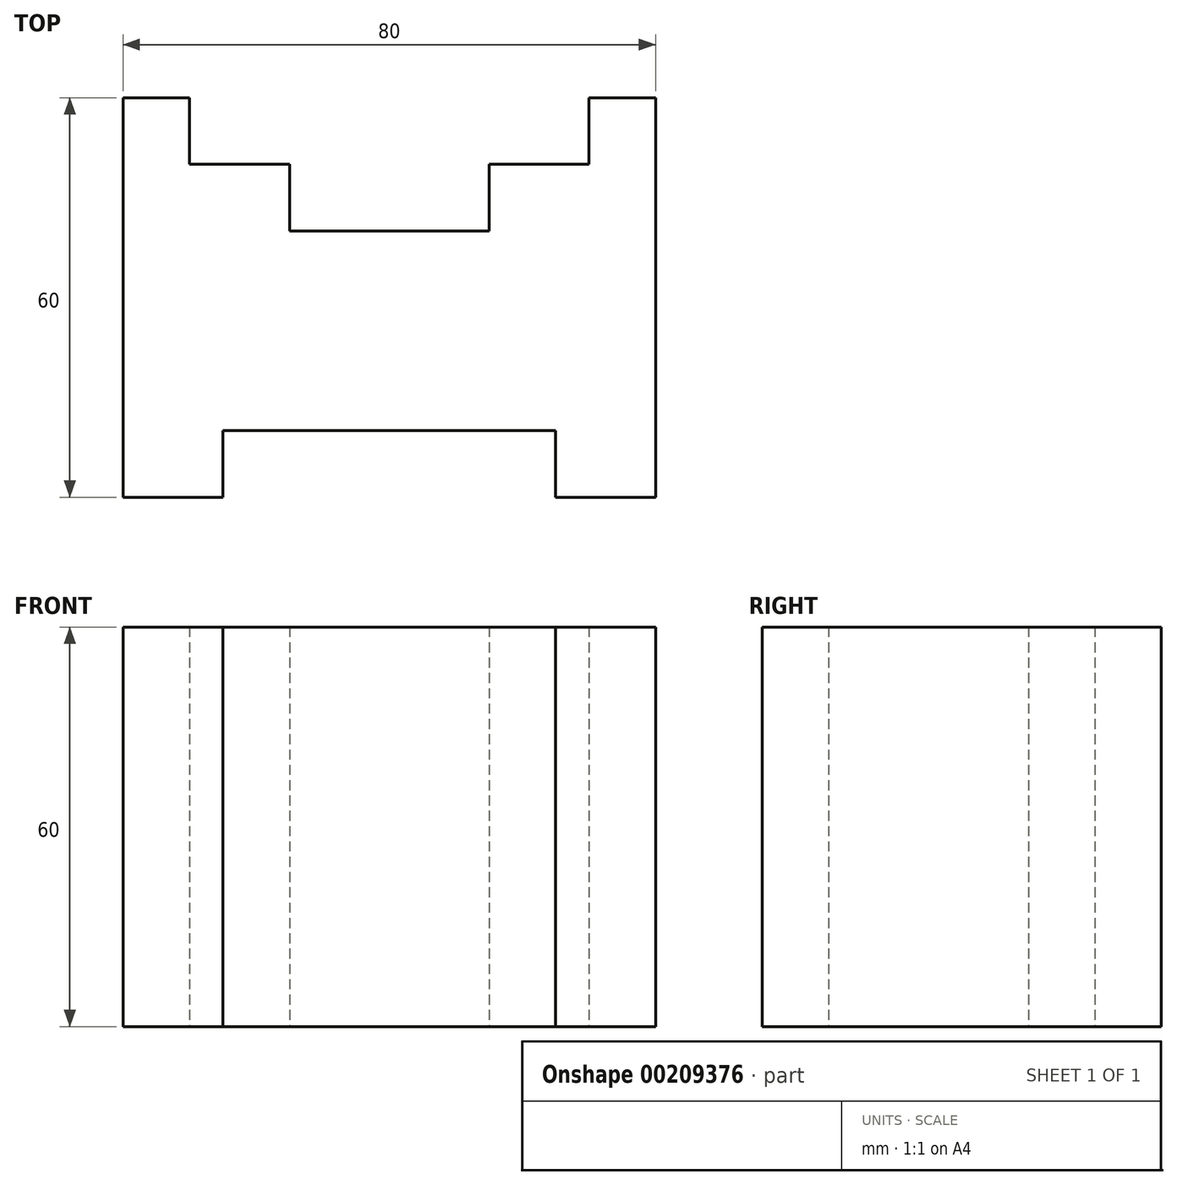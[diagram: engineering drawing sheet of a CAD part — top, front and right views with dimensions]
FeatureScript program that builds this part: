
annotation { "Feature Type Name" : "Feature", "Feature Type Description" : "" }
export const myFeature = defineFeature(function(context is Context, id is Id, definition is map)
    precondition{}
    {
        {
            var Q0;
            Q0=qCreatedBy(makeId("Top.planeOp"),FACE);
            var sketch = newSketch(context, id + "F0", { "sketchPlane" : qUnion([Q0])});
            skLineSegment(sketch, "E0", {"start": v(0, 0) * mm, "end": v(15, 0) * mm});
            skLineSegment(sketch, "E1", {"start": v(15, 0) * mm, "end": v(15, 10) * mm});
            skLineSegment(sketch, "E2", {"start": v(15, 10) * mm, "end": v(65, 10) * mm});
            skLineSegment(sketch, "E3", {"start": v(65, 10) * mm, "end": v(65, 0) * mm});
            skLineSegment(sketch, "E4", {"start": v(65, 0) * mm, "end": v(80, 0) * mm});
            skLineSegment(sketch, "E5", {"start": v(80, 0) * mm, "end": v(80, 60) * mm});
            skLineSegment(sketch, "E6", {"start": v(80, 60) * mm, "end": v(70, 60) * mm});
            skLineSegment(sketch, "E7", {"start": v(70, 60) * mm, "end": v(70, 50) * mm});
            skLineSegment(sketch, "E8", {"start": v(70, 50) * mm, "end": v(55, 50) * mm});
            skLineSegment(sketch, "E9", {"start": v(55, 50) * mm, "end": v(55, 40) * mm});
            skLineSegment(sketch, "E10", {"start": v(55, 40) * mm, "end": v(25, 40) * mm});
            skLineSegment(sketch, "E11", {"start": v(25, 40) * mm, "end": v(25, 50) * mm});
            skLineSegment(sketch, "E12", {"start": v(25, 50) * mm, "end": v(10, 50) * mm});
            skLineSegment(sketch, "E13", {"start": v(10, 50) * mm, "end": v(10, 60) * mm});
            skLineSegment(sketch, "E14", {"start": v(10, 60) * mm, "end": v(0, 60) * mm});
            skLineSegment(sketch, "E15", {"start": v(0, 60) * mm, "end": v(0, 0) * mm});
            skSolve(sketch);
        }
        {
            var Q0;
            Q0=makeQuery(id+"F0.imprint","IMPRINT",FACE,{"disambiguationData":[TD([[makeQuery(id+"F0.imprint","IMPRINT",EDGE,{"derivedFrom":sQuery(id+"F0.wireOp",EDGE,"E0")}),1.0]])]});
            extrude(context, id + "F1", {"entities" : qUnion([Q0]), "depth" : 60 * mm});
        }
    });
